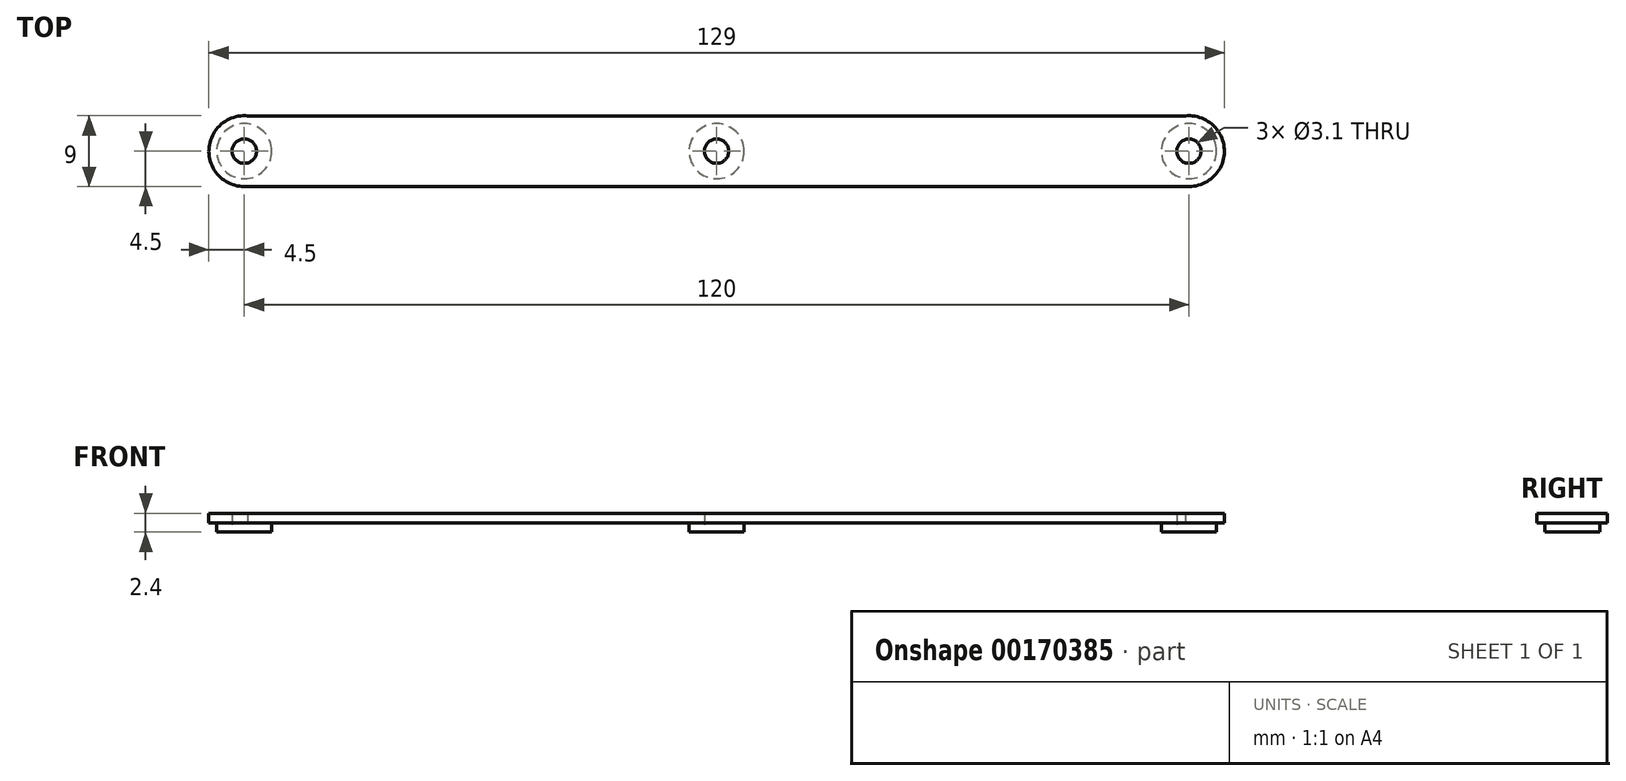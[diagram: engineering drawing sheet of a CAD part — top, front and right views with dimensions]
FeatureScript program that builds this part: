
annotation { "Feature Type Name" : "Feature", "Feature Type Description" : "" }
export const myFeature = defineFeature(function(context is Context, id is Id, definition is map)
    precondition{}
    {
        {
            var Q0;
            Q0=qCreatedBy(makeId("Top.planeOp"),FACE);
            var sketch = newSketch(context, id + "F0", { "sketchPlane" : qUnion([Q0])});
            skLineSegment(sketch, "E0.bottom", {"start": v(-59.54, 4.48) * mm, "end": v(59.54, 4.48) * mm});
            skLineSegment(sketch, "E0.top", {"start": v(-60, -4.5) * mm, "end": v(60, -4.5) * mm});
            skPoint(sketch, "E1.positionSnap0", {"position": v(0, 0) * mm});
            skCircle(sketch, "E2", {"center": v(0, 0) * mm, "radius": 1.55 * mm, "construction": true});
            skCircle(sketch, "E3", {"center": v(-60, 0) * mm, "radius": 1.55 * mm, "construction": true});
            skCircle(sketch, "E4", {"center": v(60, 0) * mm, "radius": 1.55 * mm, "construction": true});
            skArc(sketch, "E5", {"start": v(60, -4.5) * mm, "mid": v(64.5, 0.23) * mm, "end": v(59.54, 4.48) * mm});
            skArc(sketch, "E6", {"start": v(-59.54, 4.48) * mm, "mid": v(-64.5, 0.23) * mm, "end": v(-60, -4.5) * mm});
            skSolve(sketch);
        }
        {
            var Q0;
            Q0 = qSketchRegion(id + "F0", true);
            var Q1;
            Q1 = qConstructionFilter(qBodyType(qCreatedBy(id + "F0" ,EDGE), BodyType.WIRE), ConstructionObject.NO);
            extrude(context, id + "F1", {"entities" : qUnion([Q0]), "surfaceEntities" : qUnion([Q1]), "depth" : 1.2 * mm});
        }
        {
            var Q0;
            Q0=makeQuery(id+"F0.imprint","IMPRINT",FACE,{"disambiguationData":[TD([[makeQuery(id+"F0.imprint","IMPRINT",EDGE,{"derivedFrom":sQuery(id+"F0.wireOp",EDGE,"E0.bottom")}),-1.0]])]});
            var sketch = newSketch(context, id + "F2", { "sketchPlane" : qUnion([Q0])});
            skPoint(sketch, "E7.0", {"position": v(60, 0) * mm});
            skPoint(sketch, "E8.0", {"position": v(-60, 0) * mm});
            skCircle(sketch, "E9", {"center": v(-60, 0) * mm, "radius": 3.5 * mm});
            skCircle(sketch, "E10", {"center": v(0, 0) * mm, "radius": 3.5 * mm});
            skCircle(sketch, "E11", {"center": v(60, 0) * mm, "radius": 3.5 * mm});
            skSolve(sketch);
        }
        {
            var Q0;
            Q0 = qSketchRegion(id + "F2", true);
            extrude(context, id + "F3", {"entities" : qUnion([Q0]), "operationType" : NewBodyOperationType.ADD, "oppositeDirection" : true, "depth" : 1.2 * mm});
        }
        {
            var Q0;
            Q0=makeQuery(id+"F3.opExtrude","CAP_FACE",FACE,{"disambiguationData":[OSD([sQuery(id+"F2.wireOp",EDGE,"E11")])],"isStart":false});
            var sketch = newSketch(context, id + "F4", { "sketchPlane" : qUnion([Q0])});
            skCircle(sketch, "E12.0", {"center": v(60, 0) * mm, "radius": 1.55 * mm});
            skCircle(sketch, "E13.0", {"center": v(0, 0) * mm, "radius": 1.55 * mm});
            skCircle(sketch, "E14.0", {"center": v(-60, 0) * mm, "radius": 1.55 * mm});
            skSolve(sketch);
        }
        {
            var Q0;
            Q0 = qSketchRegion(id + "F4", true);
            var Q1;
            Q1=makeQuery(id+"F1.opExtrude","SWEPT_BODY",BODY,{"disambiguationData":[OSD([sQuery(id+"F0.wireOp",EDGE,"E0.bottom"),sQuery(id+"F0.wireOp",EDGE,"E0.top"),sQuery(id+"F0.wireOp",EDGE,"E5"),sQuery(id+"F0.wireOp",EDGE,"E6")])]});
            extrude(context, id + "F5", {"entities" : qUnion([Q0]), "operationType" : NewBodyOperationType.REMOVE, "endBound" : BoundingType.UP_TO_BODY, "oppositeDirection" : true, "endBoundEntityBody" : qUnion([Q1]), "depth" : 25 * mm});
        }
    });
